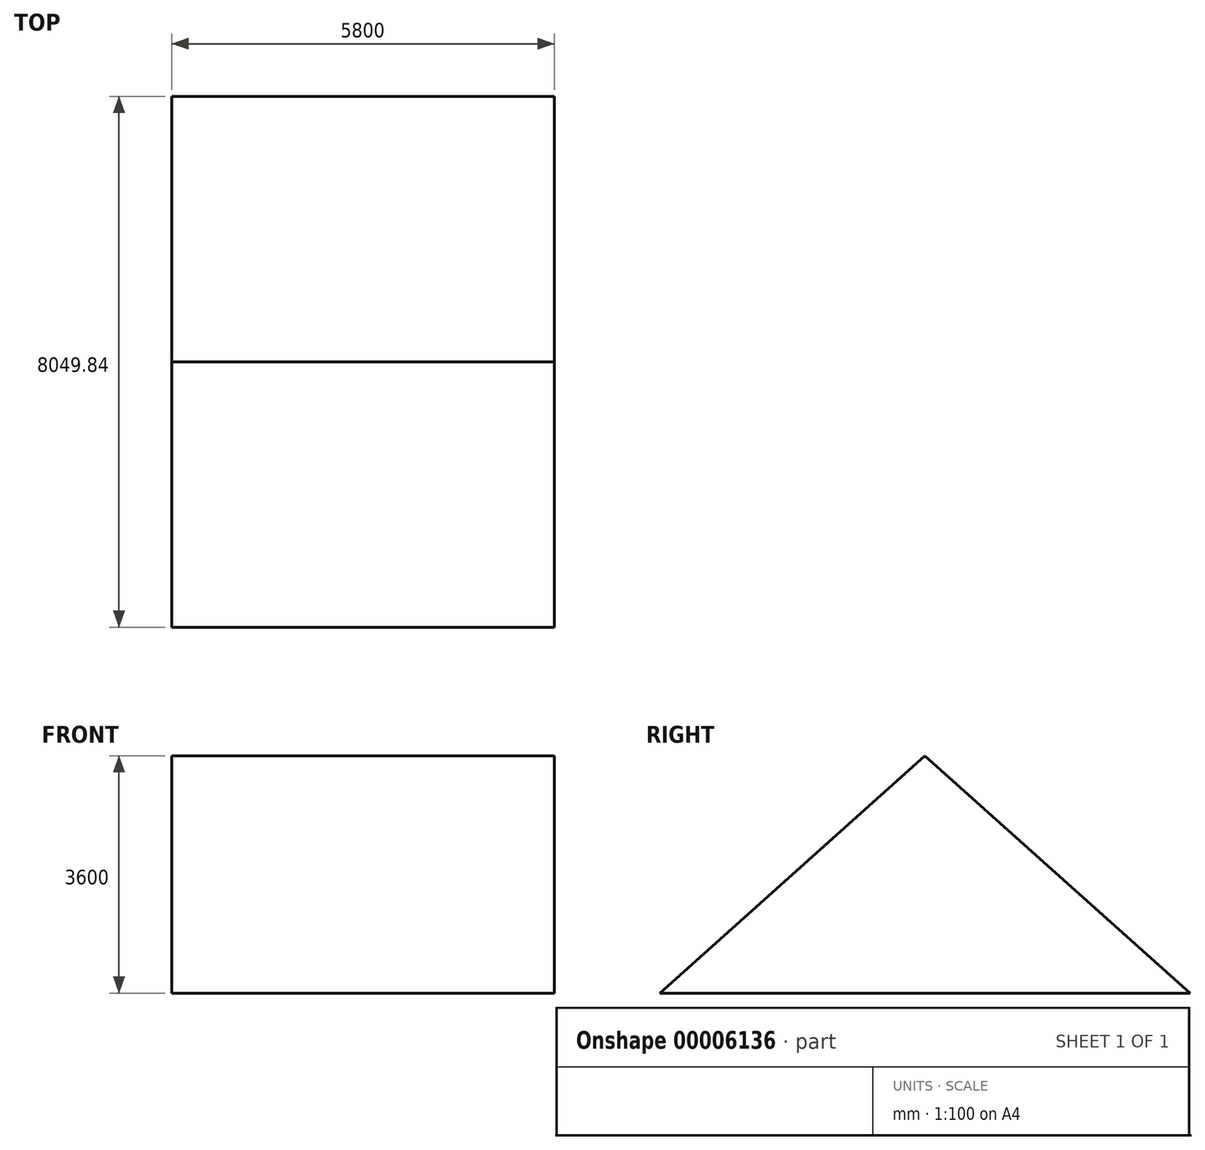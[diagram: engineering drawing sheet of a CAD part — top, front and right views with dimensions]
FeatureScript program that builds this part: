
annotation { "Feature Type Name" : "Feature", "Feature Type Description" : "" }
export const myFeature = defineFeature(function(context is Context, id is Id, definition is map)
    precondition{}
    {
        {
            var Q0;
            Q0=qCreatedBy(makeId("Right.planeOp"),FACE);
            var sketch = newSketch(context, id + "F0", { "sketchPlane" : qUnion([Q0])});
            skLineSegment(sketch, "E0", {"start": v(-4024.92, 0) * mm, "end": v(0, 3600) * mm});
            skLineSegment(sketch, "E1", {"start": v(0, 3600) * mm, "end": v(4024.92, 0) * mm});
            skLineSegment(sketch, "E2", {"start": v(4024.92, 0) * mm, "end": v(-4024.92, 0) * mm});
            skSolve(sketch);
        }
        {
            var Q0;
            Q0=makeQuery(id+"F0.imprint","IMPRINT",FACE,{"disambiguationData":[TD([[makeQuery(id+"F0.imprint","IMPRINT",EDGE,{"derivedFrom":sQuery(id+"F0.wireOp",EDGE,"E0")}),-1.0]])]});
            extrude(context, id + "F1", {"entities" : qUnion([Q0]), "depth" : 5800 * mm});
        }
    });
